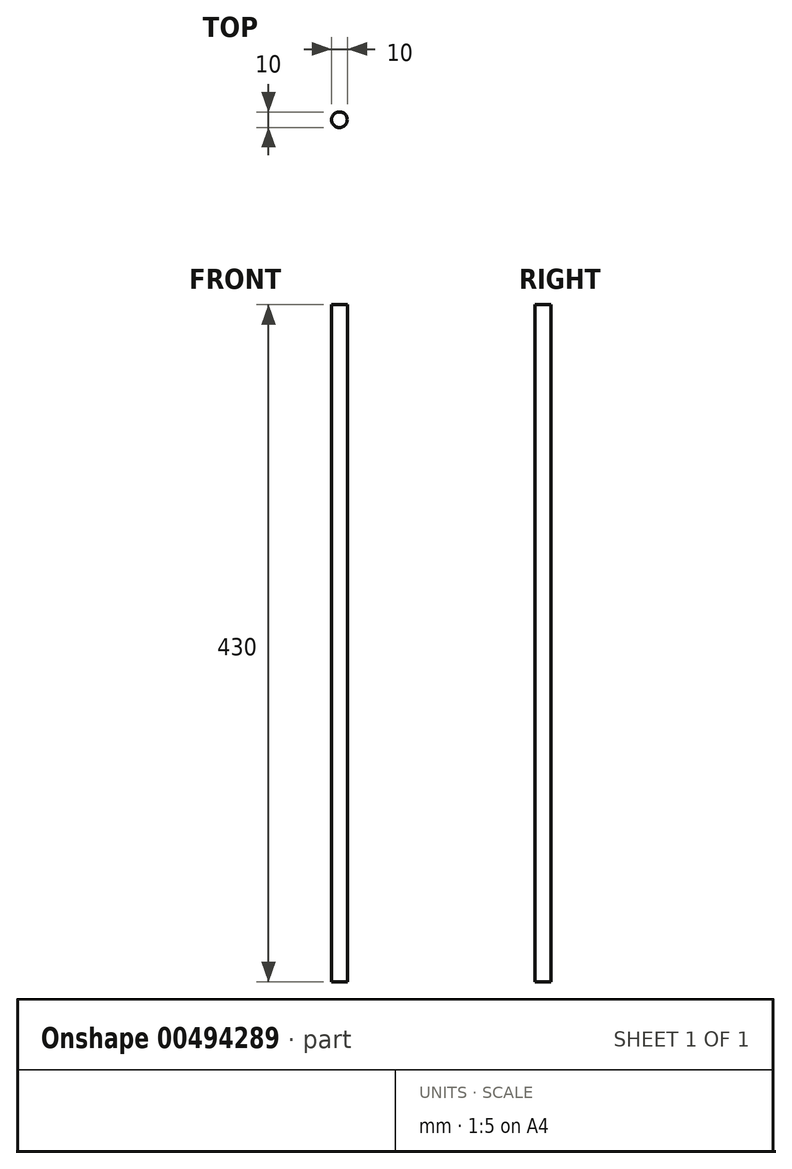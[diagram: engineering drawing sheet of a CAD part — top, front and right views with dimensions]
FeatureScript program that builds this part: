
annotation { "Feature Type Name" : "Feature", "Feature Type Description" : "" }
export const myFeature = defineFeature(function(context is Context, id is Id, definition is map)
    precondition{}
    {
        {
            var Q0;
            Q0=qCreatedBy(makeId("Top.planeOp"),FACE);
            var sketch = newSketch(context, id + "F0", { "sketchPlane" : qUnion([Q0])});
            skCircle(sketch, "E0", {"center": v(0, 0) * mm, "radius": 5 * mm});
            skSolve(sketch);
        }
        {
            var Q0;
            Q0 = qSketchRegion(id + "F0", true);
            extrude(context, id + "F1", {"entities" : qUnion([Q0]), "depth" : 430 * mm});
        }
    });
